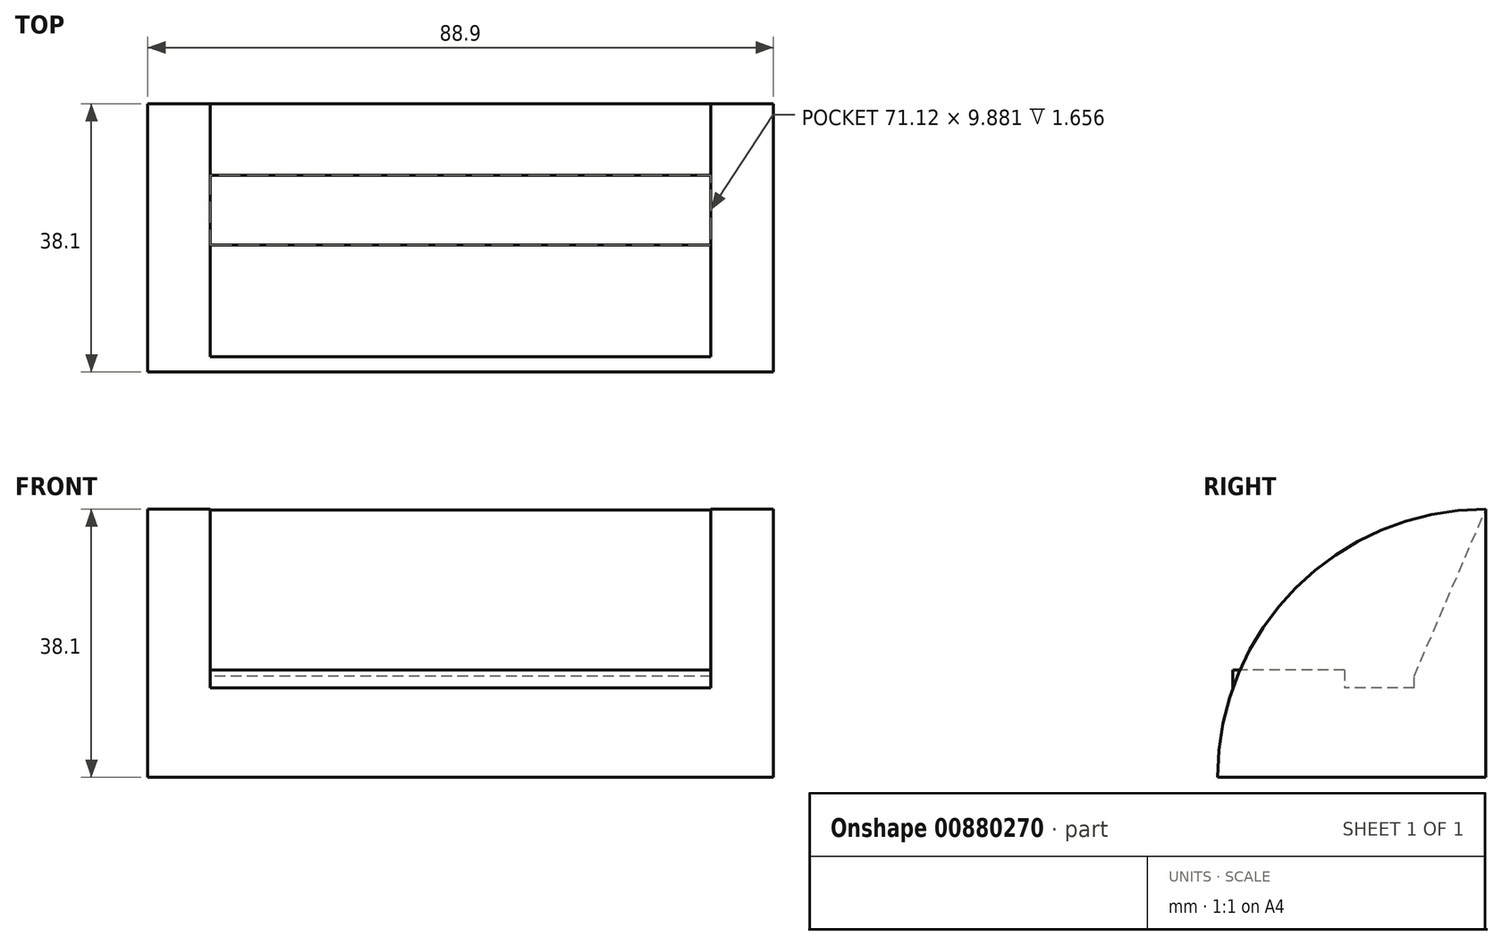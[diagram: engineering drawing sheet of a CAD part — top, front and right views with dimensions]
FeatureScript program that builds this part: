
annotation { "Feature Type Name" : "Feature", "Feature Type Description" : "" }
export const myFeature = defineFeature(function(context is Context, id is Id, definition is map)
    precondition{}
    {
        {
            var Q0;
            Q0=qCreatedBy(makeId("Top.planeOp"),FACE);
            var sketch = newSketch(context, id + "F0", { "sketchPlane" : qUnion([Q0])});
            skLineSegment(sketch, "E0.bottom", {"start": v(-44.45, 19.05) * mm, "end": v(44.45, 19.05) * mm});
            skLineSegment(sketch, "E0.top", {"start": v(-44.45, -19.05) * mm, "end": v(44.45, -19.05) * mm});
            skLineSegment(sketch, "E0.left", {"start": v(-44.45, 19.05) * mm, "end": v(-44.45, -19.05) * mm});
            skLineSegment(sketch, "E0.right", {"start": v(44.45, 19.05) * mm, "end": v(44.45, -19.05) * mm});
            skPoint(sketch, "E0.middle", {"position": v(0, 0) * mm});
            skSolve(sketch);
        }
        {
            var Q0;
            Q0=makeQuery(id+"F0.imprint","IMPRINT",FACE,{"disambiguationData":[TD([[makeQuery(id+"F0.imprint","IMPRINT",EDGE,{"derivedFrom":sQuery(id+"F0.wireOp",EDGE,"E0.bottom")}),-1.0]])]});
            extrude(context, id + "F1", {"entities" : qUnion([Q0]), "depth" : 38.1 * mm, "offsetDistance" : 25.4 * mm});
        }
        {
            var Q0;
            Q0=makeQuery(id+"F1.opExtrude","CAP_FACE",FACE,{"disambiguationData":[OSD([sQuery(id+"F0.wireOp",EDGE,"E0.bottom"),sQuery(id+"F0.wireOp",EDGE,"E0.top"),sQuery(id+"F0.wireOp",EDGE,"E0.left"),sQuery(id+"F0.wireOp",EDGE,"E0.right")])],"isStart":false});
            var sketch = newSketch(context, id + "F2", { "sketchPlane" : qUnion([Q0])});
            skLineSegment(sketch, "E1.bottom", {"start": v(-35.56, 8.9) * mm, "end": v(35.56, 8.9) * mm});
            skLineSegment(sketch, "E1.top", {"start": v(-35.56, -8.9) * mm, "end": v(35.56, -8.9) * mm});
            skLineSegment(sketch, "E1.left", {"start": v(-35.56, 8.9) * mm, "end": v(-35.56, -8.9) * mm});
            skLineSegment(sketch, "E1.right", {"start": v(35.56, 8.9) * mm, "end": v(35.56, -8.9) * mm});
            skPoint(sketch, "E1.middle", {"position": v(0, 0) * mm});
            skSolve(sketch);
        }
        {
            var Q0;
            Q0=makeQuery(id+"F2.imprint","IMPRINT",FACE,{"disambiguationData":[TD([[makeQuery(id+"F2.imprint","IMPRINT",EDGE,{"derivedFrom":sQuery(id+"F2.wireOp",EDGE,"E1.bottom")}),-1.0]])]});
            extrude(context, id + "F3", {"entities" : qUnion([Q0]), "operationType" : NewBodyOperationType.REMOVE, "oppositeDirection" : true, "depth" : 25.4 * mm, "offsetDistance" : 25.4 * mm});
        }
        {
            var Q0;
            Q0=makeQuery(id+"F1.opExtrude","CAP_EDGE",EDGE,{"disambiguationData":[OSD([sQuery(id+"F0.wireOp",EDGE,"E0.top")])],"isStart":false});
            fillet(context, id + "F4", {"entities" : qUnion([Q0]), "radius" : 38.1 * mm, "tangentPropagation" : true, "allowEdgeOverflow" : false});
        }
        {
            var Q0;
            Q0=makeQuery(id+"F4.opFillet","BLEND_EDGE",EDGE,{"blendedFrom":[makeQuery(id+"F1.opExtrude","CAP_EDGE",EDGE,{"disambiguationData":[OSD([sQuery(id+"F0.wireOp",EDGE,"E0.top")])],"isStart":false}),makeQuery(id+"F3.boolean.opBoolean","COPY",FACE,{"derivedFrom":makeQuery(id+"F3.opExtrude","SWEPT_FACE",FACE,{"disambiguationData":[OSD([sQuery(id+"F2.wireOp",EDGE,"E1.bottom")])]})})],"blendedInto":[makeQuery(id+"F3.boolean.opBoolean","COPY",FACE,{"derivedFrom":makeQuery(id+"F3.opExtrude","SWEPT_FACE",FACE,{"disambiguationData":[OSD([sQuery(id+"F2.wireOp",EDGE,"E1.bottom")])]})})]});
            chamfer(context, id + "F5", {"entities" : qUnion([Q0]), "chamferType" : ChamferType.OFFSET_ANGLE, "width" : 4 * mm, "oppositeDirection" : false, "angle" : 65 * degree, "tangentPropagation" : true});
        }
        {
            var Q0;
            Q0=makeQuery(id+"F3.boolean.opBoolean","COPY",FACE,{"derivedFrom":makeQuery(id+"F3.opExtrude","SWEPT_FACE",FACE,{"disambiguationData":[OSD([sQuery(id+"F2.wireOp",EDGE,"E1.top")])]})});
            extrude(context, id + "F6", {"entities" : qUnion([Q0]), "operationType" : NewBodyOperationType.REMOVE, "oppositeDirection" : true, "depth" : 25.4 * mm, "offsetDistance" : 25.4 * mm});
        }
        {
            var Q0;
            {var subQ0=sQuery(id+"F2.wireOp",EDGE,"E1.top");Q0=makeQuery(id+"F6.boolean.opBoolean","MERGE",FACE,{"derivedFrom":[makeQuery(id+"F3.boolean.opBoolean","COPY",FACE,{"derivedFrom":makeQuery(id+"F3.opExtrude","CAP_FACE",FACE,{"disambiguationData":[OSD([sQuery(id+"F2.wireOp",EDGE,"E1.bottom"),subQ0,sQuery(id+"F2.wireOp",EDGE,"E1.left"),sQuery(id+"F2.wireOp",EDGE,"E1.right")])],"isStart":false})})],"fromTools":[makeQuery(id+"F6.opExtrude","SWEPT_FACE",FACE,{"disambiguationData":[OSD([subQ0])]})]});}
            var sketch = newSketch(context, id + "F7", { "sketchPlane" : qUnion([Q0])});
            skLineSegment(sketch, "E2.bottom", {"start": v(-35.56, -16.87) * mm, "end": v(35.56, -16.87) * mm});
            skLineSegment(sketch, "E2.top", {"start": v(-35.56, -1) * mm, "end": v(35.56, -1) * mm});
            skLineSegment(sketch, "E2.left", {"start": v(-35.56, -16.87) * mm, "end": v(-35.56, -1) * mm});
            skLineSegment(sketch, "E2.right", {"start": v(35.56, -16.87) * mm, "end": v(35.56, -1) * mm});
            skSolve(sketch);
        }
        {
            var Q0;
            Q0=makeQuery(id+"F7.imprint","IMPRINT",FACE,{"disambiguationData":[TD([[makeQuery(id+"F7.imprint","IMPRINT",EDGE,{"derivedFrom":sQuery(id+"F7.wireOp",EDGE,"E2.bottom")}),-1.0]])]});
            extrude(context, id + "F8", {"entities" : qUnion([Q0]), "operationType" : NewBodyOperationType.ADD, "depth" : 2.54 * mm, "offsetDistance" : 25.4 * mm});
        }
    });
